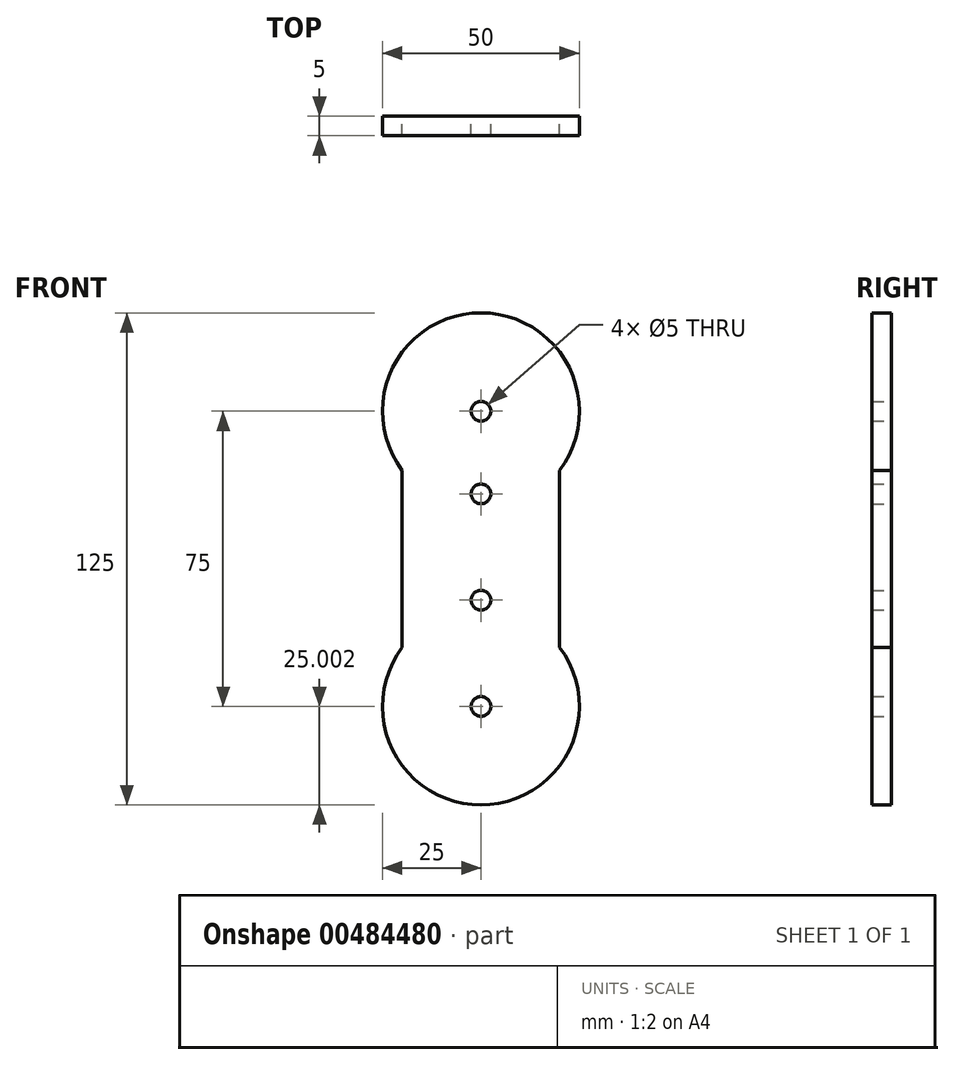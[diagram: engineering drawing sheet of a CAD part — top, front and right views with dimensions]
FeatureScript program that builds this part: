
annotation { "Feature Type Name" : "Feature", "Feature Type Description" : "" }
export const myFeature = defineFeature(function(context is Context, id is Id, definition is map)
    precondition{}
    {
        {
            var Q0;
            Q0=qCreatedBy(makeId("Front.planeOp"),FACE);
            var sketch = newSketch(context, id + "F0", { "sketchPlane" : qUnion([Q0])});
            skCircle(sketch, "E0", {"center": v(0, 47.88) * mm, "radius": 25 * mm});
            skCircle(sketch, "E1", {"center": v(0, -27.12) * mm, "radius": 25 * mm});
            skLineSegment(sketch, "E2.bottom", {"start": v(-20, 32.88) * mm, "end": v(20, 32.88) * mm});
            skLineSegment(sketch, "E2.top", {"start": v(-20, -12.12) * mm, "end": v(20, -12.12) * mm});
            skLineSegment(sketch, "E2.left", {"start": v(-20, 32.88) * mm, "end": v(-20, -12.12) * mm});
            skLineSegment(sketch, "E2.right", {"start": v(20, 32.88) * mm, "end": v(20, -12.12) * mm});
            skCircle(sketch, "E3", {"center": v(0, 47.88) * mm, "radius": 2.5 * mm});
            skCircle(sketch, "E4", {"center": v(0, 26.88) * mm, "radius": 2.5 * mm});
            skCircle(sketch, "E5", {"center": v(0, -0.12) * mm, "radius": 2.5 * mm});
            skCircle(sketch, "E6", {"center": v(0, -27.12) * mm, "radius": 2.5 * mm});
            skSolve(sketch);
        }
        {
            var Q0;
            Q0 = qSketchRegion(id + "F0", true);
            extrude(context, id + "F1", {"entities" : qUnion([Q0]), "depth" : 5 * mm});
        }
    });
